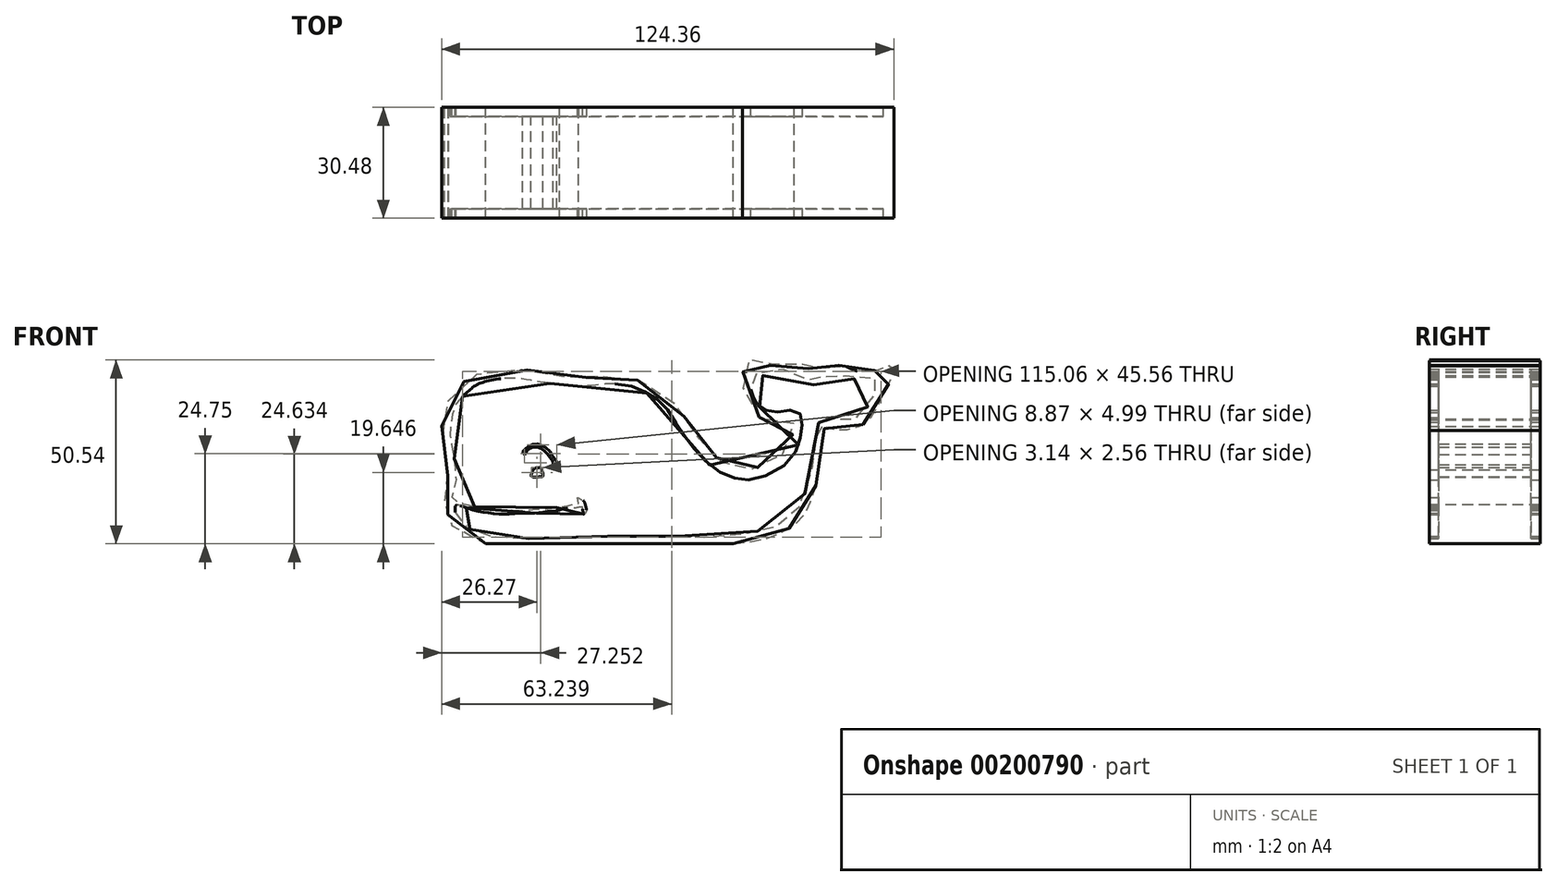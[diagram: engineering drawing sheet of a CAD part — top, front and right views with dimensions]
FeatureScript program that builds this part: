
annotation { "Feature Type Name" : "Feature", "Feature Type Description" : "" }
export const myFeature = defineFeature(function(context is Context, id is Id, definition is map)
    precondition{}
    {
        {
            var Q0;
            Q0=qCreatedBy(makeId("Front.planeOp"),FACE);
            var sketch = newSketch(context, id + "F0", { "sketchPlane" : qUnion([Q0])});
            skLineSegment(sketch, "E0", {"start": v(-105.38, 26.48) * mm, "end": v(21.62, 26.48) * mm});
            skLineSegment(sketch, "E1", {"start": v(-105.38, 26.48) * mm, "end": v(-105.38, -37.02) * mm});
            skFitSpline(sketch, "E2", {"points": [v(-92.4, 10.15) * mm, v(-82.98, 14.67) * mm, v(-71.69, 12.79) * mm, v(-57.75, 12.41) * mm, v(-42.3, 9.02) * mm, v(-32.89, -3.03) * mm, v(-19.7, -14.33) * mm, v(-6.15, -9.43) * mm, v(-3.51, 0) * mm, v(-10.67, 0) * mm, v(-16.7, 7.14) * mm, v(-15.56, 16.93) * mm, v(-11.04, 15.8) * mm, v(-4.26, 16.55) * mm, v(3.27, 12.79) * mm, v(8.54, 15.42) * mm, v(17.2, 13.16) * mm, v(22.86, 15.42) * mm, v(15.7, 0) * mm, v(6.28, 0) * mm, v(3.65, -15.46) * mm, v(0, -27.14) * mm, v(-10.67, -31.66) * mm, v(-38.16, -32.41) * mm, v(-67.17, -32.79) * mm, v(-82.23, -34.3) * mm, v(-96.17, -30.53) * mm, v(-99.56, -23.37) * mm, v(-100.31, -19.98) * mm, v(-99.18, -12.07) * mm, v(-101.06, 0) * mm, v(-98.43, 6.76) * mm, v(-92.4, 10.15) * mm]});
            skFitSpline(sketch, "E3", {"points": [v(-97.3, 4.16) * mm, v(-98.94, 1.51) * mm, v(-98.44, -3.53) * mm, v(-97.43, -9.82) * mm, v(-97.55, -14.61) * mm, v(-98.06, -19.27) * mm, v(-97.43, -21.42) * mm, v(-92.51, -22.8) * mm, v(-86.47, -23.8) * mm, v(-78.15, -24.06) * mm, v(-71.73, -23.43) * mm, v(-65.55, -22.93) * mm, v(-62.78, -22.17) * mm, v(-62.15, -21.92) * mm, v(-62.53, -21.29) * mm, v(-63.16, -20.53) * mm, v(-63.41, -20.03) * mm, v(-62.28, -20.28) * mm, v(-61.14, -22.42) * mm, v(-60.9, -23.68) * mm, v(-61.4, -25.57) * mm, v(-62.02, -24.57) * mm, v(-61.77, -23.56) * mm, v(-62.15, -23.05) * mm, v(-65.3, -23.94) * mm, v(-69.46, -24.19) * mm, v(-73.87, -24.57) * mm, v(-76.77, -24.94) * mm, v(-80.3, -25.07) * mm, v(-85.33, -24.82) * mm, v(-89.36, -24.31) * mm, v(-94.28, -23.43) * mm, v(-97.05, -22.42) * mm, v(-96.8, -25.7) * mm, v(-91, -30.1) * mm, v(-81.18, -31.75) * mm, v(-74.5, -31.62) * mm, v(-67.17, -30.49) * mm, v(-58.37, -30.87) * mm, v(-49.17, -31) * mm, v(-38.09, -31) * mm, v(-26.62, -30.74) * mm, v(-15.66, -29.98) * mm, v(-6.84, -28.1) * mm, v(-2.18, -25.2) * mm, v(0, -19.53) * mm, v(1.6, -13.35) * mm, v(2.48, -5.54) * mm, v(3.5, 0) * mm, v(4.62, 1.39) * mm, v(8.15, 1.64) * mm, v(12.56, 0) * mm, v(16.85, 3.03) * mm, v(20, 7.69) * mm, v(21.38, 12.35) * mm, v(21.38, 13.1) * mm, v(19.24, 12.1) * mm, v(15.46, 11.22) * mm, v(12.18, 12.73) * mm, v(11.43, 12.48) * mm, v(9.03, 13.36) * mm, v(6.28, 12.1) * mm, v(1.85, 10.84) * mm, v(-1.17, 12.6) * mm, v(-3.56, 14.37) * mm, v(-6.71, 14.74) * mm, v(-9.49, 13.6) * mm, v(-11.12, 13.6) * mm, v(-12.89, 12.98) * mm, v(-14.9, 14.11) * mm, v(-14.53, 7.44) * mm, v(-10.62, 3.9) * mm, v(-5.83, 3.9) * mm, v(-1.3, 1.14) * mm, v(-2.68, -7.8) * mm, v(-7.85, -14.36) * mm, v(-16.8, -16.88) * mm, v(-26.62, -13.23) * mm, v(-34.43, -4.91) * mm, v(-39.35, 2.65) * mm, v(-46.78, 8.82) * mm, v(-57.49, 10.33) * mm, v(-67.17, 10.46) * mm, v(-74, 11.47) * mm, v(-80.92, 12.48) * mm, v(-87.85, 10.59) * mm, v(-94.78, 6.3) * mm, v(-96.2, 5.17) * mm, v(-96.71, 4.65) * mm, v(-97.3, 4.16) * mm]});
            skFitSpline(sketch, "E4", {"points": [v(-76.04, -14.23) * mm, v(-75.76, -13.16) * mm, v(-75.26, -12.28) * mm, v(-74.67, -11.93) * mm, v(-73.95, -11.8) * mm, v(-73.38, -12.14) * mm, v(-72.86, -12.9) * mm, v(-72.57, -14.1) * mm, v(-72.59, -14.4) * mm, v(-74.33, -14.55) * mm, v(-75.58, -14.5) * mm, v(-76, -14.5) * mm, v(-76.04, -14.23) * mm]});
            skFitSpline(sketch, "E5", {"points": [v(-77.8, -8.12) * mm, v(-77.28, -7.59) * mm, v(-76.69, -7.04) * mm, v(-75.87, -6.67) * mm, v(-75.11, -6.44) * mm, v(-74.13, -6.44) * mm, v(-73.4, -6.71) * mm, v(-72.7, -7.26) * mm, v(-71.56, -8.33) * mm, v(-70.79, -9.46) * mm, v(-70.03, -10.71) * mm, v(-69.63, -11.3) * mm, v(-69, -11.08) * mm, v(-69.61, -10.03) * mm, v(-70.3, -8.93) * mm, v(-70.86, -8.18) * mm, v(-71.47, -7.5) * mm, v(-72.13, -6.82) * mm, v(-73.31, -6.13) * mm, v(-74.6, -5.88) * mm, v(-75.56, -6.03) * mm, v(-76.45, -6.4) * mm, v(-77.4, -6.96) * mm, v(-78.2, -7.75) * mm, v(-78.2, -8.29) * mm, v(-77.8, -8.12) * mm]});
            skFitSpline(sketch, "E6", {"points": [v(49.5, 80.83) * mm, v(48.07, 79.3) * mm, v(46.96, 76.42) * mm, v(46.45, 74.46) * mm, v(46.28, 71.07) * mm, v(46.11, 69.28) * mm, v(46.7, 67.08) * mm, v(47.22, 64.02) * mm, v(47.56, 60.03) * mm, v(47.73, 57.4) * mm, v(47.22, 55.27) * mm, v(46.62, 53.92) * mm, v(46.96, 52.39) * mm, v(48.66, 51.62) * mm, v(51.38, 50.94) * mm, v(54.69, 50) * mm, v(58, 49.67) * mm, v(62.33, 49.59) * mm, v(66.66, 49.5) * mm, v(71.75, 49.92) * mm, v(75.4, 50.18) * mm, v(77.36, 50.86) * mm, v(80.92, 51.03) * mm, v(81.52, 51.62) * mm, v(81.18, 52.56) * mm, v(81.26, 53.07) * mm, v(82.2, 52.73) * mm, v(83.13, 51.62) * mm, v(83.64, 49.67) * mm, v(83.64, 49.42) * mm, v(82.96, 48.4) * mm, v(82.62, 49.59) * mm, v(82.62, 50) * mm, v(82.49, 50.38) * mm, v(79.88, 50.07) * mm, v(78.39, 50.13) * mm, v(76.5, 49.72) * mm, v(75.3, 49.4) * mm, v(73.3, 49.2) * mm, v(70.97, 48.92) * mm, v(68.84, 48.7) * mm, v(66.48, 48.68) * mm, v(63.12, 48.58) * mm, v(60, 48.47) * mm, v(56.81, 48.8) * mm, v(54.14, 49.16) * mm, v(50.67, 50.2) * mm, v(49.21, 50.68) * mm, v(48.38, 50.96) * mm, v(47.8, 50.91) * mm, v(47.52, 50.33) * mm, v(47.52, 49.4) * mm, v(47.5, 48.06) * mm, v(47.67, 47.28) * mm, v(48.1, 46.62) * mm, v(49.16, 45.71) * mm, v(50.17, 45) * mm, v(51.3, 44.42) * mm, v(52.82, 43.62) * mm, v(54.66, 42.83) * mm, v(56.53, 42.53) * mm, v(58.63, 42.15) * mm, v(61.12, 41.92) * mm, v(62.8, 41.75) * mm, v(64.97, 41.8) * mm, v(67.85, 41.8) * mm, v(70.91, 41.7) * mm, v(73.88, 42) * mm, v(77.07, 42.18) * mm, v(79.78, 42.18) * mm, v(85.51, 42.18) * mm, v(89.89, 42.39) * mm, v(92.82, 42.39) * mm, v(96.13, 42.39) * mm, v(98.46, 42.35) * mm, v(101.4, 42.3) * mm, v(103.81, 42.26) * mm, v(107.46, 42.35) * mm, v(110.14, 42.35) * mm, v(114.21, 42.22) * mm, v(118.33, 42.18) * mm, v(122.32, 42.52) * mm, v(126.48, 42.98) * mm, v(129.96, 43.7) * mm, v(132.64, 44.09) * mm, v(134.8, 44.8) * mm, v(137.26, 45.64) * mm, v(139.3, 46.97) * mm, v(141.04, 48.78) * mm, v(142.22, 50.67) * mm, v(143.24, 53.02) * mm, v(144.37, 55.93) * mm, v(145.66, 60.89) * mm, v(145.85, 63.42) * mm, v(146.33, 67.58) * mm, v(146.94, 69.78) * mm, v(147.2, 71.58) * mm, v(147.48, 73.5) * mm, v(148.08, 74.77) * mm, v(148.71, 75.02) * mm, v(150.22, 74.53) * mm, v(150.56, 74.37) * mm, v(152.83, 73.83) * mm, v(155.57, 73.9) * mm, v(158.27, 75.02) * mm, v(160.16, 76.69) * mm, v(161.33, 78.69) * mm, v(162.63, 80.78) * mm, v(164.25, 83.19) * mm, v(165.13, 84.71) * mm, v(165.04, 85.77) * mm, v(163.56, 85.82) * mm, v(162.16, 85.5) * mm, v(158.38, 85.5) * mm, v(156.34, 85.84) * mm, v(155.03, 86.31) * mm, v(153.66, 86.78) * mm, v(152.33, 86.96) * mm, v(151.05, 86.96) * mm, v(149.9, 86.78) * mm, v(148.6, 86.15) * mm, v(147.4, 85.43) * mm, v(146.76, 84.47) * mm, v(146.46, 84.02) * mm, v(146.01, 84) * mm, v(145.11, 84.78) * mm, v(144.03, 86) * mm, v(141.99, 87.37) * mm, v(140.44, 88.16) * mm, v(138.32, 88.36) * mm, v(137, 87.98) * mm, v(134.75, 87.14) * mm, v(132.4, 86.6) * mm, v(130.6, 86.92) * mm, v(129.78, 87.64) * mm, v(129.28, 87.7) * mm, v(128.88, 86.8) * mm, v(128.8, 85.07) * mm, v(128.79, 83.39) * mm, v(129.2, 81.16) * mm, v(129.78, 80.04) * mm, v(130.65, 78.6) * mm, v(131.69, 77.6) * mm, v(134.79, 76.46) * mm, v(138.02, 76.96) * mm, v(141.45, 76.76) * mm, v(142.97, 74.95) * mm, v(142.66, 71.51) * mm, v(141.89, 67.4) * mm, v(138.26, 62.1) * mm, v(129.94, 58.17) * mm, v(125.4, 58.17) * mm, v(120.1, 60.13) * mm, v(114.5, 64.97) * mm, v(111.18, 69.2) * mm, v(108, 73.9) * mm, v(104.97, 78.44) * mm, v(101.04, 81.31) * mm, v(97.1, 83.28) * mm, v(91.2, 84.34) * mm, v(85.6, 83.88) * mm, v(80.16, 83.73) * mm, v(73.05, 84.49) * mm, v(67.45, 85.4) * mm, v(61.4, 85.85) * mm, v(54.9, 84.64) * mm, v(52.33, 83.28) * mm, v(49.5, 80.83) * mm]});
            skFitSpline(sketch, "E7", {"points": [v(43.9, 72.27) * mm, v(44.2, 68.08) * mm, v(44.82, 64.95) * mm, v(45.37, 61.41) * mm, v(45.52, 58.13) * mm, v(45.12, 56.11) * mm, v(44.46, 52.63) * mm, v(45.17, 51.03) * mm, v(45.57, 51.03) * mm, v(45.52, 47.88) * mm, v(46.18, 46.07) * mm, v(48.5, 43.29) * mm, v(52.54, 41.52) * mm, v(57.08, 40.06) * mm, v(62.64, 39.7) * mm, v(66.58, 39.65) * mm, v(71.47, 39.7) * mm, v(76.52, 40.36) * mm, v(84.4, 40.16) * mm, v(88.54, 40.1) * mm, v(94.24, 40.3) * mm, v(99.5, 40.2) * mm, v(104.04, 40.2) * mm, v(109.19, 40.06) * mm, v(114.08, 40.06) * mm, v(117.82, 39.8) * mm, v(123.17, 40.22) * mm, v(128.14, 40.81) * mm, v(133.06, 41.72) * mm, v(136.92, 43.33) * mm, v(141.46, 45.95) * mm, v(143.82, 48.62) * mm, v(144.83, 51.03) * mm, v(146.44, 55.04) * mm, v(147.19, 59.8) * mm, v(148.36, 65.68) * mm, v(148.68, 69.86) * mm, v(149.23, 72.33) * mm, v(149.97, 72.39) * mm, v(151.44, 71.82) * mm, v(154.1, 71.48) * mm, v(157.1, 72.16) * mm, v(160.34, 73.58) * mm, v(162.72, 76.47) * mm, v(163.74, 78.34) * mm, v(165.15, 81.4) * mm, v(166.91, 84.57) * mm, v(168.04, 87.35) * mm, v(168.04, 88.7) * mm, v(167.25, 89.28) * mm, v(165.44, 88.65) * mm, v(163.28, 88.03) * mm, v(161.64, 87.75) * mm, v(160, 87.63) * mm, v(157.28, 88.03) * mm, v(155.92, 88.65) * mm, v(154.16, 89.33) * mm, v(152, 89.39) * mm, v(149.97, 89.28) * mm, v(148.1, 88.65) * mm, v(146.9, 88.09) * mm, v(146, 87.3) * mm, v(145.2, 88.09) * mm, v(143.68, 89.16) * mm, v(142.6, 89.96) * mm, v(141.18, 90.47) * mm, v(138.01, 90.47) * mm, v(134.84, 89.62) * mm, v(132.85, 89.1) * mm, v(131.1, 89.33) * mm, v(129.74, 90.52) * mm, v(127.81, 90.75) * mm, v(127.07, 89.67) * mm, v(126.56, 86.1) * mm, v(126.73, 82.87) * mm, v(127.75, 78.73) * mm, v(130.08, 76.13) * mm, v(132.51, 74.43) * mm, v(138.35, 74.48) * mm, v(140.33, 74.2) * mm, v(140.56, 72.44) * mm, v(140.16, 69.33) * mm, v(138.63, 65.98) * mm, v(135.4, 63.5) * mm, v(132.46, 61.9) * mm, v(129.45, 60.88) * mm, v(127.02, 60.54) * mm, v(124.24, 60.88) * mm, v(121.63, 62.13) * mm, v(119.14, 64.23) * mm, v(117.04, 66.21) * mm, v(115.29, 68.48) * mm, v(112.06, 72.56) * mm, v(109.4, 77.03) * mm, v(105.7, 80.83) * mm, v(101.12, 83.95) * mm, v(97.5, 85.37) * mm, v(94.26, 86.33) * mm, v(89.33, 86.27) * mm, v(87.18, 86.1) * mm, v(81.8, 86.1) * mm, v(77.77, 86.22) * mm, v(73.7, 87.07) * mm, v(67.46, 88.03) * mm, v(61.62, 88.2) * mm, v(55.39, 87.52) * mm, v(50.06, 85.03) * mm, v(47.23, 82.2) * mm, v(44.85, 78.28) * mm, v(43.83, 74.65) * mm, v(43.9, 72.27) * mm]});
            skFitSpline(sketch, "E8", {"points": [v(68.5, 58.84) * mm, v(68.74, 60.07) * mm, v(69.2, 60.87) * mm, v(70.18, 61.22) * mm, v(70.9, 61.16) * mm, v(71.44, 60.36) * mm, v(71.57, 58.8) * mm, v(71.23, 58.73) * mm, v(70.53, 58.73) * mm, v(68.5, 58.84) * mm]});
            skFitSpline(sketch, "E9", {"points": [v(66.62, 64.92) * mm, v(67.17, 65.8) * mm, v(68, 66.49) * mm, v(68.95, 66.85) * mm, v(70.12, 66.91) * mm, v(71.12, 66.47) * mm, v(72.07, 65.8) * mm, v(73.03, 64.87) * mm, v(73.7, 63.9) * mm, v(74.5, 62.84) * mm, v(74.47, 62.35) * mm, v(75.26, 62.14) * mm, v(75.49, 62.64) * mm, v(75.34, 63.2) * mm, v(75.06, 63.5) * mm, v(74.15, 64.73) * mm, v(73.28, 66.06) * mm, v(71.48, 67.3) * mm, v(70.3, 67.74) * mm, v(68.8, 67.63) * mm, v(67.55, 67.08) * mm, v(66.64, 66.27) * mm, v(66.09, 65.45) * mm, v(66.62, 64.92) * mm]});
            skSolve(sketch);
        }
        {
            var Q0;
            Q0=makeQuery(id+"F0.imprint","IMPRINT",FACE,{"disambiguationData":[TD([[makeQuery(id+"F0.imprint","IMPRINT",EDGE,{"derivedFrom":sQuery(id+"F0.wireOp",EDGE,"E6")}),1.0]])]});
            extrude(context, id + "F1", {"entities" : qUnion([Q0]), "depth" : 25.4 * mm});
        }
        {
            var Q0;
            Q0=makeQuery(id+"F0.imprint","IMPRINT",FACE,{"disambiguationData":[TD([[makeQuery(id+"F0.imprint","IMPRINT",EDGE,{"derivedFrom":sQuery(id+"F0.wireOp",EDGE,"E6")}),-1.0]])]});
            var Q1;
            Q1=sQuery(id+"F0.wireOp",EDGE,"E7");
            extrude(context, id + "F2", {"entities" : qUnion([Q0]), "surfaceEntities" : qUnion([Q1]), "depth" : 27.94 * mm});
        }
        {
            var Q0;
            Q0=makeQuery(id+"F2.opExtrude","CAP_FACE",FACE,{"disambiguationData":[OSD([sQuery(id+"F0.wireOp",EDGE,"E6"),sQuery(id+"F0.wireOp",EDGE,"E7")])],"isStart":true});
            extrude(context, id + "F3", {"entities" : qUnion([Q0]), "operationType" : NewBodyOperationType.ADD, "depth" : 2.54 * mm});
        }
        {
            var Q0;
            Q0=makeQuery(id+"F2.opExtrude","CAP_FACE",FACE,{"disambiguationData":[OSD([sQuery(id+"F0.wireOp",EDGE,"E6"),sQuery(id+"F0.wireOp",EDGE,"E7")])],"isStart":false});
            var sketch = newSketch(context, id + "F4", { "sketchPlane" : qUnion([Q0])});
            skLineSegment(sketch, "E10.bottom", {"start": v(53.27, 40.32) * mm, "end": v(137.66, 40.32) * mm});
            skLineSegment(sketch, "E10.top", {"start": v(53.27, 37.75) * mm, "end": v(137.66, 37.75) * mm});
            skLineSegment(sketch, "E10.left", {"start": v(53.27, 40.32) * mm, "end": v(53.27, 37.75) * mm});
            skLineSegment(sketch, "E10.right", {"start": v(137.66, 40.32) * mm, "end": v(137.66, 37.75) * mm});
            skSolve(sketch);
        }
        {
            var Q0;
            {var subQ0=sQuery(id+"F4.wireOp",EDGE,"E10.bottom");var subQ1=makeQuery(id+"F2.opExtrude","CAP_EDGE",EDGE,{"disambiguationData":[OSD([sQuery(id+"F0.wireOp",EDGE,"E7")])],"isStart":false});var subQ2=makeQuery(id+"F4.imprint","INTERSECT",VERTEX,{"disambiguationData":[OD(0.0)],"derivedFrom":[subQ1,subQ0]});Q0=makeQuery(id+"F4.imprint","IMPRINT",FACE,{"disambiguationData":[TD([[makeQuery(id+"F4.imprint","IMPRINT",EDGE,{"disambiguationData":[TD([[subQ2,-1.0]])],"derivedFrom":subQ0}),-1.0]])]});}
            var Q1;
            {var subQ0=sQuery(id+"F4.wireOp",EDGE,"E10.bottom");var subQ1=makeQuery(id+"F2.opExtrude","CAP_EDGE",EDGE,{"disambiguationData":[OSD([sQuery(id+"F0.wireOp",EDGE,"E7")])],"isStart":false});var subQ2=makeQuery(id+"F4.imprint","INTERSECT",VERTEX,{"disambiguationData":[OD(2.0)],"derivedFrom":[subQ1,subQ0]});Q1=makeQuery(id+"F4.imprint","IMPRINT",FACE,{"disambiguationData":[TD([[makeQuery(id+"F4.imprint","IMPRINT",EDGE,{"disambiguationData":[TD([[subQ2,-1.0]])],"derivedFrom":subQ0}),1.0]])]});}
            var Q2;
            {var subQ0=sQuery(id+"F4.wireOp",EDGE,"E10.bottom");var subQ1=makeQuery(id+"F2.opExtrude","CAP_EDGE",EDGE,{"disambiguationData":[OSD([sQuery(id+"F0.wireOp",EDGE,"E7")])],"isStart":false});var subQ2=makeQuery(id+"F4.imprint","INTERSECT",VERTEX,{"disambiguationData":[OD(1.0)],"derivedFrom":[subQ1,subQ0]});Q2=makeQuery(id+"F4.imprint","IMPRINT",FACE,{"disambiguationData":[TD([[makeQuery(id+"F4.imprint","IMPRINT",EDGE,{"disambiguationData":[TD([[subQ2,1.0]])],"derivedFrom":subQ0}),-1.0]])]});}
            var Q3;
            Q3=makeQuery(id+"F4.imprint","IMPRINT",FACE,{"disambiguationData":[TD([[makeQuery(id+"F4.imprint","IMPRINT",EDGE,{"derivedFrom":sQuery(id+"F4.wireOp",EDGE,"E10.top")}),1.0]])]});
            extrude(context, id + "F5", {"entities" : qUnion([Q0, Q1, Q2, Q3]), "operationType" : NewBodyOperationType.REMOVE, "endBound" : BoundingType.THROUGH_ALL, "oppositeDirection" : true, "depth" : 25.4 * mm});
        }
    });
